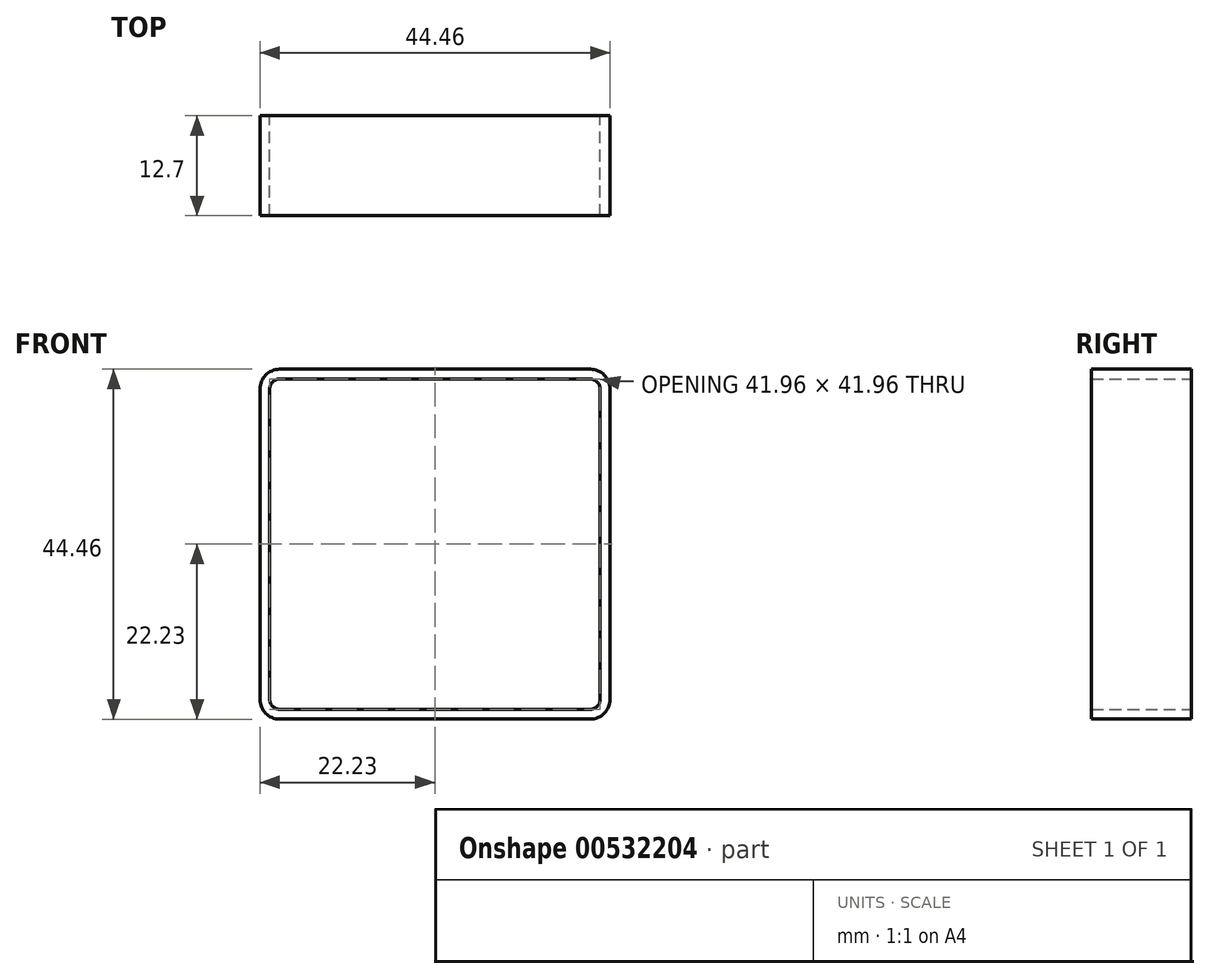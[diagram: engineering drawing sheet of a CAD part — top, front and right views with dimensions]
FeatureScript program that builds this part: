
annotation { "Feature Type Name" : "Feature", "Feature Type Description" : "" }
export const myFeature = defineFeature(function(context is Context, id is Id, definition is map)
    precondition{}
    {
        {
            var Q0;
            Q0=qCreatedBy(makeId("Front.planeOp"),FACE);
            var sketch = newSketch(context, id + "F0", { "sketchPlane" : qUnion([Q0])});
            skLineSegment(sketch, "E0.bottom", {"start": v(19.74, 22.23) * mm, "end": v(-19.74, 22.22) * mm});
            skLineSegment(sketch, "E0.top", {"start": v(19.74, -22.22) * mm, "end": v(-19.74, -22.23) * mm});
            skLineSegment(sketch, "E0.left", {"start": v(22.22, 19.74) * mm, "end": v(22.23, -19.74) * mm});
            skLineSegment(sketch, "E0.right", {"start": v(-22.23, 19.74) * mm, "end": v(-22.22, -19.74) * mm});
            skPoint(sketch, "E0.middle", {"position": v(0, 0) * mm});
            skLineSegment(sketch, "E1.bottom", {"start": v(19.74, 20.98) * mm, "end": v(-19.74, 20.98) * mm});
            skLineSegment(sketch, "E1.top", {"start": v(19.74, -20.98) * mm, "end": v(-19.74, -20.98) * mm});
            skLineSegment(sketch, "E1.left", {"start": v(20.98, 19.74) * mm, "end": v(20.98, -19.74) * mm});
            skLineSegment(sketch, "E1.right", {"start": v(-20.98, 19.74) * mm, "end": v(-20.98, -19.74) * mm});
            skPoint(sketch, "E2.visualSharp", {"position": v(20.98, 20.98) * mm});
            skArc(sketch, "E2.filletArc", {"start": v(20.98, 19.74) * mm, "mid": v(20.62, 20.62) * mm, "end": v(19.74, 20.98) * mm});
            skPoint(sketch, "E3.visualSharp", {"position": v(-20.98, 20.98) * mm});
            skArc(sketch, "E3.filletArc", {"start": v(-19.74, 20.98) * mm, "mid": v(-20.62, 20.62) * mm, "end": v(-20.98, 19.74) * mm});
            skPoint(sketch, "E4.visualSharp", {"position": v(-20.98, -20.98) * mm});
            skArc(sketch, "E4.filletArc", {"start": v(-20.98, -19.74) * mm, "mid": v(-20.62, -20.62) * mm, "end": v(-19.74, -20.98) * mm});
            skPoint(sketch, "E5.visualSharp", {"position": v(20.98, -20.98) * mm});
            skArc(sketch, "E5.filletArc", {"start": v(19.74, -20.98) * mm, "mid": v(20.62, -20.62) * mm, "end": v(20.98, -19.74) * mm});
            skPoint(sketch, "E6.visualSharp", {"position": v(-22.23, 22.22) * mm});
            skArc(sketch, "E6.filletArc", {"start": v(-19.74, 22.22) * mm, "mid": v(-21.5, 21.5) * mm, "end": v(-22.23, 19.74) * mm});
            skPoint(sketch, "E7.visualSharp", {"position": v(22.22, 22.23) * mm});
            skArc(sketch, "E7.filletArc", {"start": v(22.22, 19.74) * mm, "mid": v(21.5, 21.5) * mm, "end": v(19.74, 22.23) * mm});
            skPoint(sketch, "E8.visualSharp", {"position": v(22.23, -22.22) * mm});
            skArc(sketch, "E8.filletArc", {"start": v(19.74, -22.22) * mm, "mid": v(21.5, -21.5) * mm, "end": v(22.23, -19.74) * mm});
            skPoint(sketch, "E9.visualSharp", {"position": v(-22.22, -22.23) * mm});
            skArc(sketch, "E9.filletArc", {"start": v(-22.22, -19.74) * mm, "mid": v(-21.5, -21.5) * mm, "end": v(-19.74, -22.23) * mm});
            skSolve(sketch);
        }
        {
            var Q0;
            Q0 = qSketchRegion(id + "F0", true);
            extrude(context, id + "F1", {"entities" : qUnion([Q0]), "depth" : 12.7 * mm, "offsetDistance" : 25.4 * mm});
        }
    });
